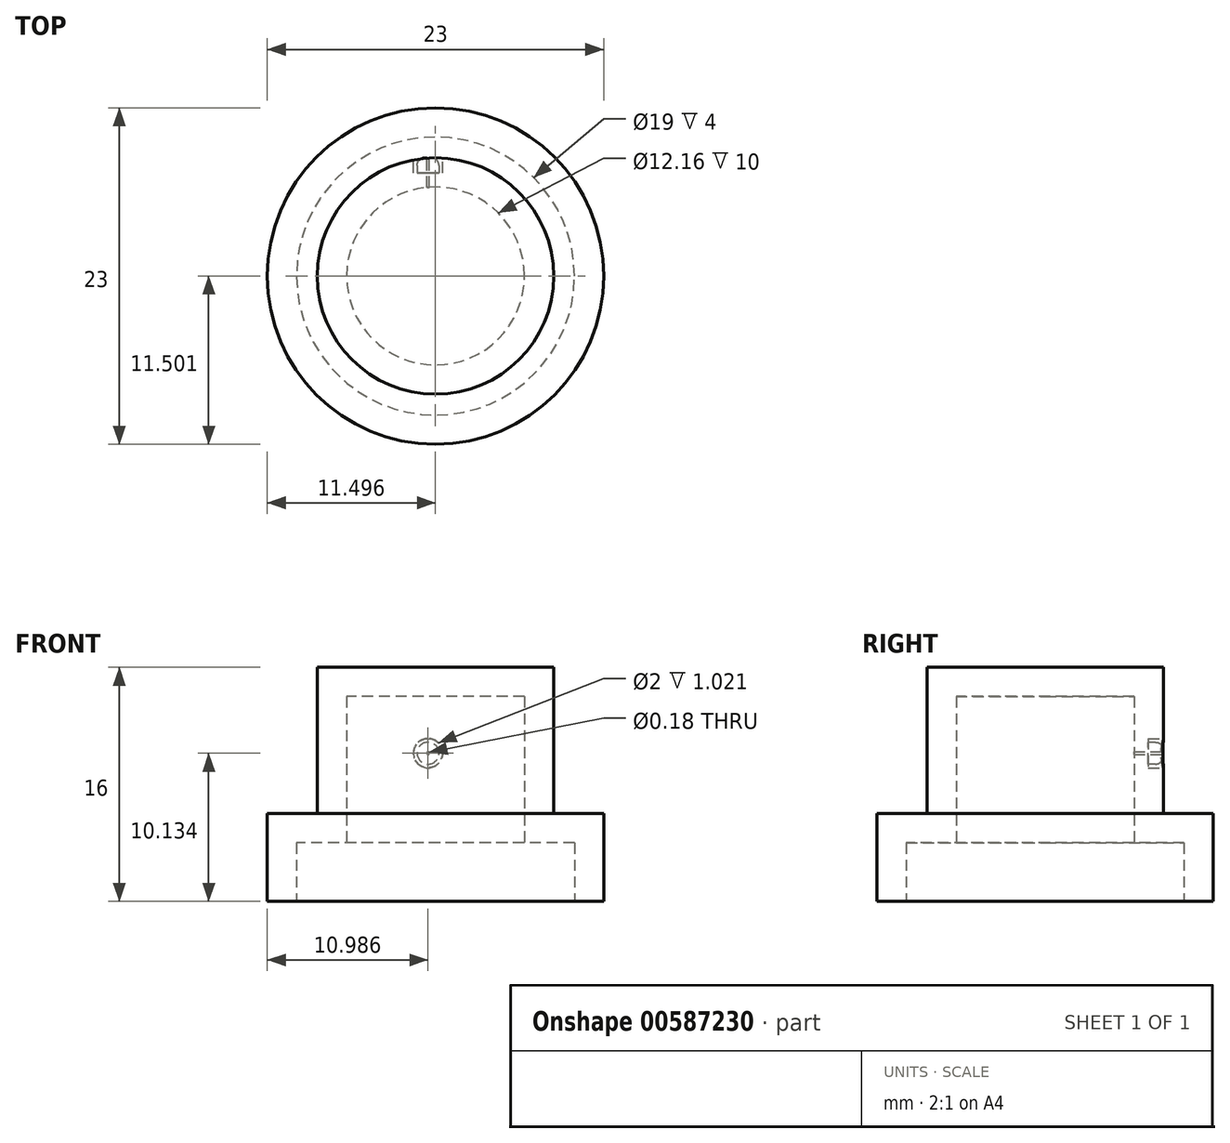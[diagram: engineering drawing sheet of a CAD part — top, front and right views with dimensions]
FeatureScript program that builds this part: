
annotation { "Feature Type Name" : "Feature", "Feature Type Description" : "" }
export const myFeature = defineFeature(function(context is Context, id is Id, definition is map)
    precondition{}
    {
        {
            var Q0;
            Q0=qCreatedBy(makeId("Top.planeOp"),FACE);
            var sketch = newSketch(context, id + "F0", { "sketchPlane" : qUnion([Q0])});
            skCircle(sketch, "E0", {"center": v(-24.42, 15.64) * mm, "radius": 11.5 * mm});
            skSolve(sketch);
        }
        {
            var Q0;
            Q0=makeQuery(id+"F0.imprint","IMPRINT",FACE,{"disambiguationData":[TD([[makeQuery(id+"F0.imprint","IMPRINT",EDGE,{"derivedFrom":sQuery(id+"F0.wireOp",EDGE,"E0")}),1.0]])]});
            extrude(context, id + "F1", {"entities" : qUnion([Q0]), "depth" : 6 * mm, "offsetDistance" : 25 * mm});
        }
        {
            var Q0;
            Q0=makeQuery(id+"F1.opExtrude","CAP_FACE",FACE,{"disambiguationData":[OSD([sQuery(id+"F0.wireOp",EDGE,"E0")])],"isStart":true});
            shell(context, id + "F2", {"entities" : qUnion([Q0]), "thickness" : 2 * mm});
        }
        {
            var Q0;
            Q0=makeQuery(id+"F1.opExtrude","CAP_FACE",FACE,{"disambiguationData":[OSD([sQuery(id+"F0.wireOp",EDGE,"E0")])],"isStart":false});
            var sketch = newSketch(context, id + "F3", { "sketchPlane" : qUnion([Q0])});
            skCircle(sketch, "E1", {"center": v(-24.42, 15.64) * mm, "radius": 8.08 * mm});
            skSolve(sketch);
        }
        {
            var Q0;
            Q0=makeQuery(id+"F3.imprint","IMPRINT",FACE,{"disambiguationData":[TD([[makeQuery(id+"F3.imprint","IMPRINT",EDGE,{"derivedFrom":sQuery(id+"F3.wireOp",EDGE,"E1")}),1.0]])]});
            extrude(context, id + "F4", {"entities" : qUnion([Q0]), "operationType" : NewBodyOperationType.ADD, "depth" : 10 * mm, "offsetDistance" : 25 * mm});
        }
        {
            var Q0;
            {var subQ0=sQuery(id+"F0.wireOp",EDGE,"E0");Q0=makeQuery(id+"F2.opShell","OFFSET_FACE",FACE,{"disambiguationData":[OSD([subQ0]),TDD([makeQuery(id+"F1.opExtrude","CAP_FACE",FACE,{"disambiguationData":[OSD([subQ0])],"isStart":false})])]});}
            shell(context, id + "F5", {"entities" : qUnion([Q0]), "thickness" : 2 * mm});
        }
        {
            var Q0;
            Q0=qCreatedBy(makeId("Front.planeOp"),FACE);
            cPlane(context, id + "F6", {"entities" : qUnion([Q0]), "cplaneType" : CPlaneType.OFFSET, "offset" : 29.7 * mm, "oppositeDirection" : true, "width" : 150 * mm, "height" : 150 * mm});
        }
        {
            var Q0;
            Q0=qCreatedBy(id+"F6.planeOp",FACE);
            var sketch = newSketch(context, id + "F7", { "sketchPlane" : qUnion([Q0])});
            skCircle(sketch, "E2", {"center": v(-24.93, 10.13) * mm, "radius": 1 * mm});
            skSolve(sketch);
        }
        {
            var Q0;
            Q0=makeQuery(id+"F7.imprint","IMPRINT",FACE,{"disambiguationData":[TD([[makeQuery(id+"F7.imprint","IMPRINT",EDGE,{"derivedFrom":sQuery(id+"F7.wireOp",EDGE,"E2")}),1.0]])]});
            extrude(context, id + "F8", {"entities" : qUnion([Q0]), "operationType" : NewBodyOperationType.REMOVE, "depth" : 7 * mm, "offsetDistance" : 25 * mm});
        }
        {
            var Q0;
            Q0=makeQuery(id+"F8.boolean.opBoolean","COPY",FACE,{"derivedFrom":makeQuery(id+"F8.opExtrude","CAP_FACE",FACE,{"disambiguationData":[OSD([sQuery(id+"F7.wireOp",EDGE,"E2")])],"isStart":false})});
            var sketch = newSketch(context, id + "F9", { "sketchPlane" : qUnion([Q0])});
            skCircle(sketch, "E3", {"center": v(24.93, 10.13) * mm, "radius": 0.75 * mm});
            skSolve(sketch);
        }
        {
            var Q0;
            Q0=makeQuery(id+"F9.imprint","IMPRINT",FACE,{"disambiguationData":[TD([[makeQuery(id+"F9.imprint","IMPRINT",EDGE,{"derivedFrom":sQuery(id+"F9.wireOp",EDGE,"E3")}),1.0]])]});
            extrude(context, id + "F10", {"entities" : qUnion([Q0]), "operationType" : NewBodyOperationType.ADD, "depth" : 1 * mm, "offsetDistance" : 25 * mm});
        }
        {
            var Q0;
            Q0=makeQuery(id+"F10.opExtrude","CAP_FACE",FACE,{"disambiguationData":[OSD([sQuery(id+"F9.wireOp",EDGE,"E3")])],"isStart":false});
            fillet(context, id + "F11", {"entities" : qUnion([Q0]), "radius" : .5 * mm, "tangentPropagation" : true, "allowEdgeOverflow" : false});
        }
        {
            var Q0;
            Q0=makeQuery(id+"F10.opExtrude","CAP_FACE",FACE,{"disambiguationData":[OSD([sQuery(id+"F9.wireOp",EDGE,"E3")])],"isStart":false});
            var sketch = newSketch(context, id + "F12", { "sketchPlane" : qUnion([Q0])});
            skCircle(sketch, "E4", {"center": v(24.93, 10.13) * mm, "radius": 0.09 * mm});
            skSolve(sketch);
        }
        {
            var Q0;
            Q0=makeQuery(id+"F12.imprint","IMPRINT",FACE,{"disambiguationData":[TD([[makeQuery(id+"F12.imprint","IMPRINT",EDGE,{"derivedFrom":sQuery(id+"F12.wireOp",EDGE,"E4")}),1.0]])]});
            extrude(context, id + "F13", {"entities" : qUnion([Q0]), "operationType" : NewBodyOperationType.REMOVE, "oppositeDirection" : true, "depth" : 7 * mm, "offsetDistance" : 25 * mm});
        }
    });
